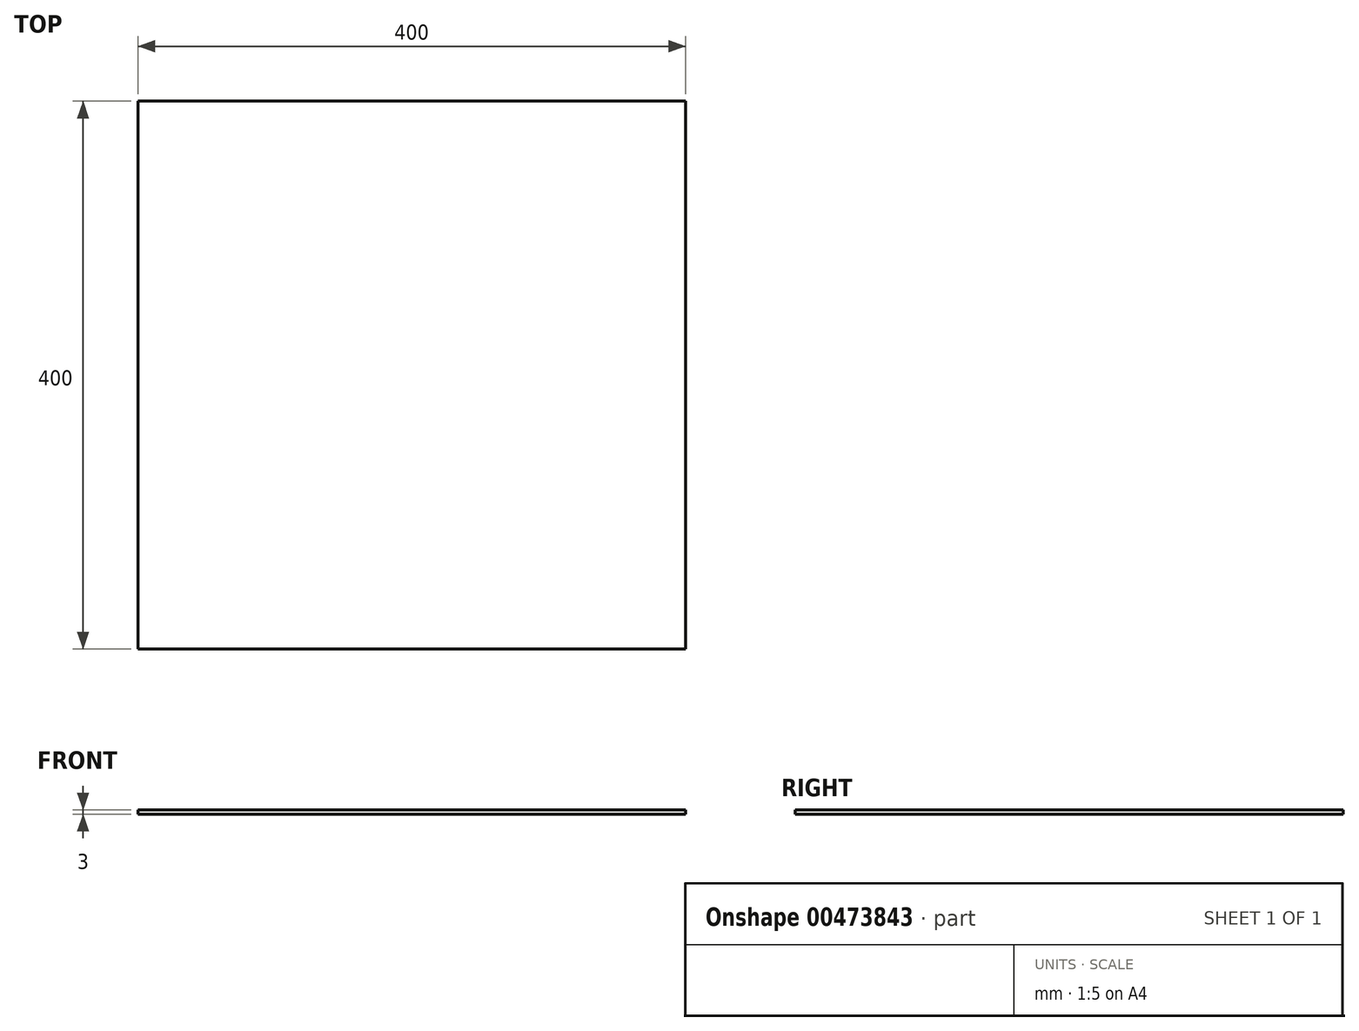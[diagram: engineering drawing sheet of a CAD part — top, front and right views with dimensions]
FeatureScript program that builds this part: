
annotation { "Feature Type Name" : "Feature", "Feature Type Description" : "" }
export const myFeature = defineFeature(function(context is Context, id is Id, definition is map)
    precondition{}
    {
        {
            var Q0;
            Q0=qCreatedBy(makeId("Top.planeOp"),FACE);
            var sketch = newSketch(context, id + "F0", { "sketchPlane" : qUnion([Q0])});
            skLineSegment(sketch, "E0.bottom", {"start": v(200, -200) * mm, "end": v(-200, -200) * mm});
            skLineSegment(sketch, "E0.top", {"start": v(200, 200) * mm, "end": v(-200, 200) * mm});
            skLineSegment(sketch, "E0.left", {"start": v(200, -200) * mm, "end": v(200, 200) * mm});
            skLineSegment(sketch, "E0.right", {"start": v(-200, -200) * mm, "end": v(-200, 200) * mm});
            skPoint(sketch, "E0.middle", {"position": v(0, 0) * mm});
            skSolve(sketch);
        }
        {
            var Q0;
            Q0=makeQuery(id+"F0.imprint","IMPRINT",FACE,{"disambiguationData":[TD([[makeQuery(id+"F0.imprint","IMPRINT",EDGE,{"derivedFrom":sQuery(id+"F0.wireOp",EDGE,"E0.bottom")}),-1.0]])]});
            extrude(context, id + "F1", {"entities" : qUnion([Q0]), "depth" : 3 * mm});
        }
    });
